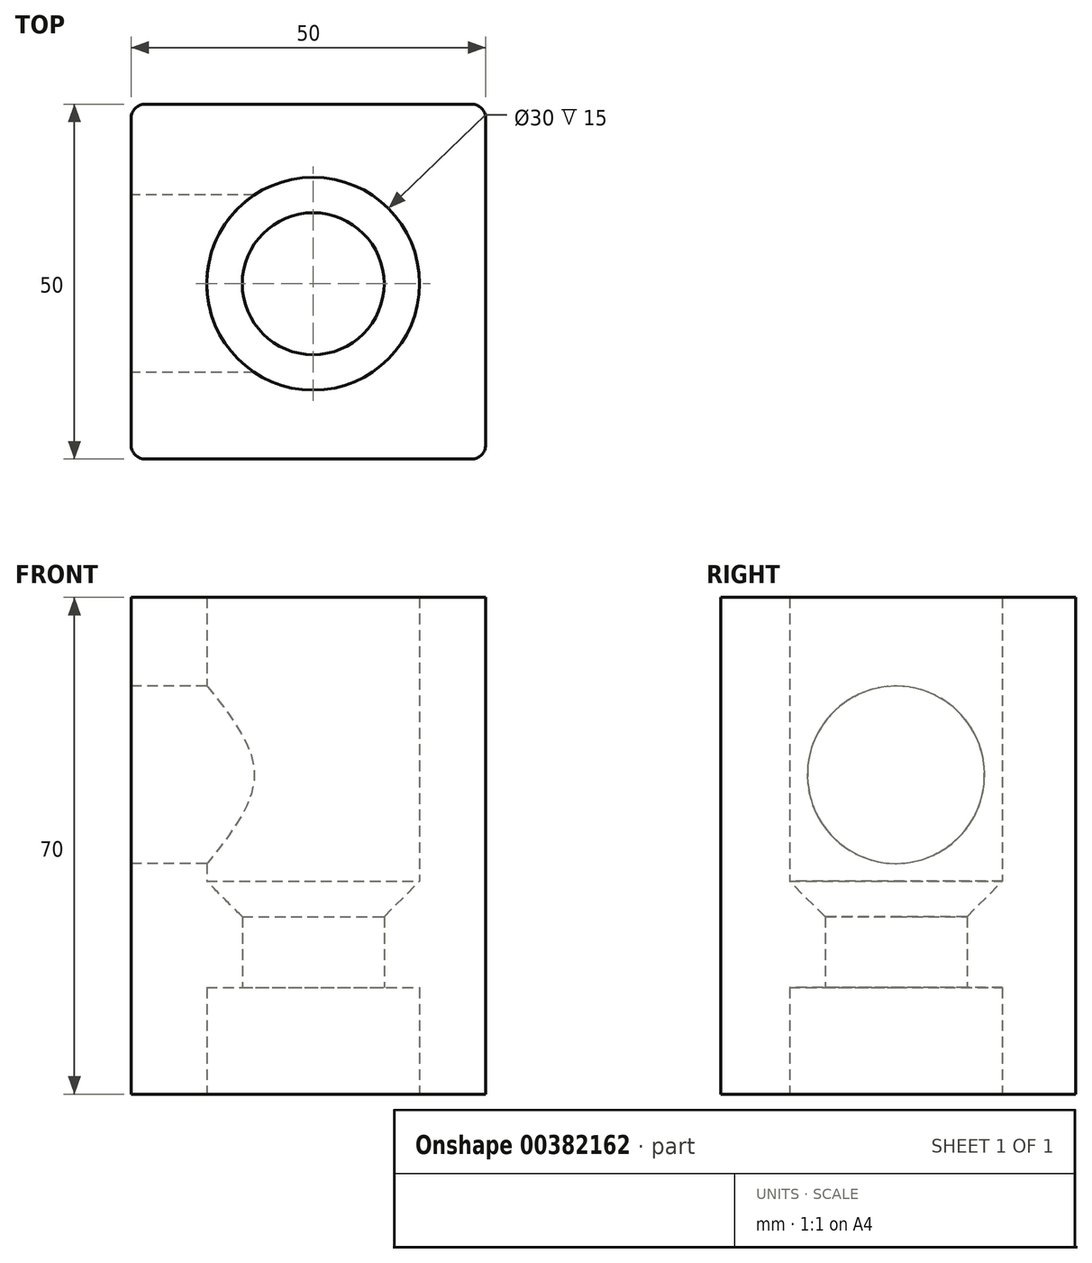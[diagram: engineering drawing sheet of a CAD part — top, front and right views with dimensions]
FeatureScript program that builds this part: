
annotation { "Feature Type Name" : "Feature", "Feature Type Description" : "" }
export const myFeature = defineFeature(function(context is Context, id is Id, definition is map)
    precondition{}
    {
        {
            var Q0;
            Q0=qCreatedBy(makeId("Top.planeOp"),FACE);
            var sketch = newSketch(context, id + "F0", { "sketchPlane" : qUnion([Q0])});
            skLineSegment(sketch, "E0.bottom", {"start": v(-25.67, 25.3) * mm, "end": v(24.33, 25.3) * mm});
            skLineSegment(sketch, "E0.top", {"start": v(-25.67, -24.7) * mm, "end": v(24.33, -24.7) * mm});
            skLineSegment(sketch, "E0.left", {"start": v(-25.67, 25.3) * mm, "end": v(-25.67, -24.7) * mm});
            skLineSegment(sketch, "E0.right", {"start": v(24.33, 25.3) * mm, "end": v(24.33, -24.7) * mm});
            skSolve(sketch);
        }
        {
            var Q0;
            Q0 = qSketchRegion(id + "F0", true);
            extrude(context, id + "F1", {"entities" : qUnion([Q0]), "depth" : 70 * mm});
        }
        {
            var Q0;
            Q0=qCreatedBy(makeId("Front.planeOp"),FACE);
            var sketch = newSketch(context, id + "F2", { "sketchPlane" : qUnion([Q0])});
            skLineSegment(sketch, "E1", {"start": v(0, 82.2) * mm, "end": v(0, 0) * mm, "construction": true});
            skLineSegment(sketch, "E2", {"start": v(-15, 70) * mm, "end": v(-15, 30) * mm});
            skLineSegment(sketch, "E3", {"start": v(-15, 30) * mm, "end": v(-10, 25) * mm});
            skLineSegment(sketch, "E4", {"start": v(-10, 25) * mm, "end": v(-10, 15) * mm});
            skLineSegment(sketch, "E5", {"start": v(-10, 15) * mm, "end": v(-15, 15) * mm});
            skLineSegment(sketch, "E6", {"start": v(-15, 15) * mm, "end": v(-15, 0) * mm});
            skLineSegment(sketch, "E7", {"start": v(-15, 70) * mm, "end": v(0, 70) * mm});
            skLineSegment(sketch, "E8", {"start": v(0, 70) * mm, "end": v(0, 0) * mm});
            skLineSegment(sketch, "E9", {"start": v(-15, 0) * mm, "end": v(0, 0) * mm});
            skSolve(sketch);
        }
        {
            var Q0;
            Q0 = qSketchRegion(id + "F2", true);
            var Q1;
            Q1=sQuery(id+"F2.wireOp",EDGE,"E1");
            revolve(context, id + "F3", {"operationType" : NewBodyOperationType.REMOVE, "entities" : qUnion([Q0]), "axis" : qUnion([Q1]), "revolveType" : RevolveType.FULL, "oppositeDirection" : true});
        }
        {
            var Q0;
            Q0=makeQuery(id+"F1.opExtrude","SWEPT_FACE",FACE,{"disambiguationData":[OSD([sQuery(id+"F0.wireOp",EDGE,"E0.left")])]});
            var sketch = newSketch(context, id + "F4", { "sketchPlane" : qUnion([Q0])});
            skCircle(sketch, "E10", {"center": v(0, 45) * mm, "radius": 12.5 * mm});
            skSolve(sketch);
        }
        {
            var Q0;
            Q0 = qSketchRegion(id + "F4", true);
            extrude(context, id + "F5", {"entities" : qUnion([Q0]), "operationType" : NewBodyOperationType.REMOVE, "oppositeDirection" : true, "depth" : 25 * mm});
        }
        {
            var Q0;
            Q0=makeQuery(id+"F1.opExtrude","SWEPT_EDGE",EDGE,{"disambiguationData":[OSD([sQuery(id+"F0.wireOp",EDGE,"E0.bottom"),sQuery(id+"F0.wireOp",EDGE,"E0.left")])]});
            var Q1;
            Q1=makeQuery(id+"F1.opExtrude","SWEPT_EDGE",EDGE,{"disambiguationData":[OSD([sQuery(id+"F0.wireOp",EDGE,"E0.bottom"),sQuery(id+"F0.wireOp",EDGE,"E0.right")])]});
            var Q2;
            Q2=makeQuery(id+"F1.opExtrude","SWEPT_EDGE",EDGE,{"disambiguationData":[OSD([sQuery(id+"F0.wireOp",EDGE,"E0.top"),sQuery(id+"F0.wireOp",EDGE,"E0.right")])]});
            var Q3;
            Q3=makeQuery(id+"F1.opExtrude","SWEPT_EDGE",EDGE,{"disambiguationData":[OSD([sQuery(id+"F0.wireOp",EDGE,"E0.top"),sQuery(id+"F0.wireOp",EDGE,"E0.left")])]});
            fillet(context, id + "F6", {"entities" : qUnion([Q0, Q1, Q2, Q3]), "radius" : 2 * mm, "tangentPropagation" : true, "allowEdgeOverflow" : false});
        }
    });
